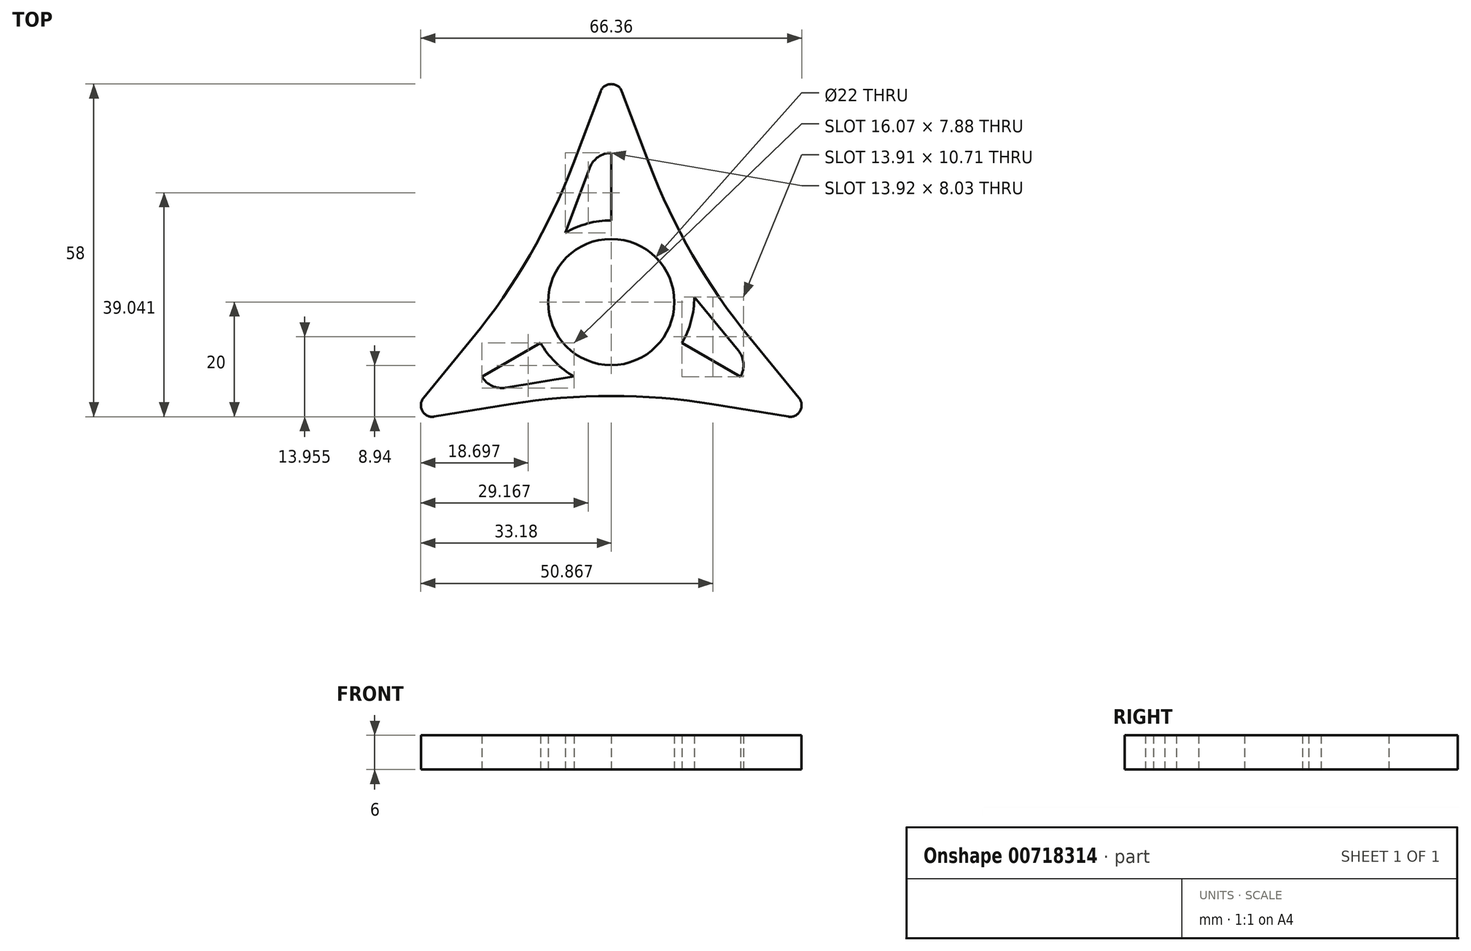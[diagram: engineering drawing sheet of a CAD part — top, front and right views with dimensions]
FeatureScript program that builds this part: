
annotation { "Feature Type Name" : "Feature", "Feature Type Description" : "" }
export const myFeature = defineFeature(function(context is Context, id is Id, definition is map)
    precondition{}
    {
        {
            var Q0;
            Q0=qCreatedBy(makeId("Top.planeOp"),FACE);
            var sketch = newSketch(context, id + "F0", { "sketchPlane" : qUnion([Q0])});
            skLineSegment(sketch, "E0", {"start": v(0, 36) * mm, "end": v(0, -37) * mm, "construction": true});
            skCircle(sketch, "E1", {"center": v(0, 0) * mm, "radius": 11 * mm});
            skCircle(sketch, "E2", {"center": v(0, 36) * mm, "radius": 2 * mm});
            skLineSegment(sketch, "E3", {"start": v(-1.87, 36.7) * mm, "end": v(-6.63, 24.1) * mm});
            skLineSegment(sketch, "E4.MirrorCS", {"start": v(1.87, 36.7) * mm, "end": v(6.63, 24.1) * mm});
            skLineSegment(sketch, "E5.1.0", {"start": v(-32.72, -16.73) * mm, "end": v(-24.2, -6.3) * mm});
            skLineSegment(sketch, "E5.1.1", {"start": v(-30.85, -19.97) * mm, "end": v(-17.56, -17.8) * mm});
            skCircle(sketch, "E5.1.2", {"center": v(-31.18, -18) * mm, "radius": 2 * mm});
            skLineSegment(sketch, "E5.2.0", {"start": v(30.85, -19.97) * mm, "end": v(17.56, -17.8) * mm});
            skLineSegment(sketch, "E5.2.1", {"start": v(32.72, -16.73) * mm, "end": v(24.2, -6.3) * mm});
            skCircle(sketch, "E5.2.2", {"center": v(31.18, -18) * mm, "radius": 2 * mm});
            skArc(sketch, "E6", {"start": v(-24.2, -6.3) * mm, "mid": v(-14.18, 8.19) * mm, "end": v(-6.63, 24.1) * mm});
            skArc(sketch, "E7.1.0", {"start": v(17.56, -17.8) * mm, "mid": v(0, -16.37) * mm, "end": v(-17.56, -17.8) * mm});
            skArc(sketch, "E7.2.0", {"start": v(6.63, 24.1) * mm, "mid": v(14.18, 8.19) * mm, "end": v(24.2, -6.3) * mm});
            skPoint(sketch, "E8.trimOffspring.end.orphan", {"position": v(-15.86, 3.15) * mm});
            skLineSegment(sketch, "E9.trimOffspring", {"start": v(-1.35, -14.7) * mm, "end": v(-3.63, -14.33) * mm});
            skLineSegment(sketch, "E10.trimOffspring", {"start": v(1.35, -14.7) * mm, "end": v(3.63, -14.33) * mm});
            skPoint(sketch, "E11.trimOffspring.end.orphan", {"position": v(15.86, 3.15) * mm});
            skArc(sketch, "E12", {"start": v(0, 26) * mm, "mid": v(-2.27, 25.3) * mm, "end": v(-3.74, 23.41) * mm});
            skLineSegment(sketch, "E13", {"start": v(-3.74, 23.41) * mm, "end": v(-8.03, 12.08) * mm});
            skPoint(sketch, "E14.MirrorCS.end.orphan", {"position": v(8.03, 12.08) * mm});
            skPoint(sketch, "E15.orphan", {"position": v(3.74, 23.41) * mm});
            skLineSegment(sketch, "E16", {"start": v(0, 26) * mm, "end": v(0, 14.24) * mm});
            skArc(sketch, "E17.trimOffspring", {"start": v(0, 14.24) * mm, "mid": v(-4.16, 13.7) * mm, "end": v(-8.03, 12.08) * mm});
            skArc(sketch, "E18.trimOffspring", {"start": v(-1.35, -14.7) * mm, "mid": v(0, -14.76) * mm, "end": v(1.35, -14.7) * mm});
            skArc(sketch, "E19.1.0", {"start": v(-22.52, -13) * mm, "mid": v(-20.77, -14.61) * mm, "end": v(-18.4, -14.95) * mm});
            skLineSegment(sketch, "E19.1.1", {"start": v(-18.4, -14.95) * mm, "end": v(-6.45, -13) * mm});
            skArc(sketch, "E19.1.2", {"start": v(-12.33, -7.12) * mm, "mid": v(-9.78, -10.44) * mm, "end": v(-6.45, -13) * mm});
            skArc(sketch, "E19.2.0", {"start": v(22.52, -13) * mm, "mid": v(23.04, -10.68) * mm, "end": v(22.15, -8.47) * mm});
            skLineSegment(sketch, "E19.2.1", {"start": v(22.15, -8.47) * mm, "end": v(14.48, 0.9) * mm});
            skArc(sketch, "E19.2.2", {"start": v(12.33, -7.12) * mm, "mid": v(13.93, -3.25) * mm, "end": v(14.48, 0.9) * mm});
            skLineSegment(sketch, "E20", {"start": v(12.33, -7.12) * mm, "end": v(22.52, -13) * mm});
            skLineSegment(sketch, "E21", {"start": v(-22.52, -13) * mm, "end": v(-12.33, -7.12) * mm});
            skSolve(sketch);
        }
        {
            var Q0;
            {var subQ18=sQuery(id+"F0.wireOp",EDGE,"E3");Q0=makeQuery(id+"F0.imprint","IMPRINT",FACE,{"disambiguationData":[TD([[makeQuery(id+"F0.imprint","IMPRINT",EDGE,{"derivedFrom":subQ18}),1.0]])]});}
            var Q1;
            {var subQ0=sQuery(id+"F0.wireOp",EDGE,"E2");var subQ1=makeQuery(id+"F0.imprint","INTERSECT",VERTEX,{"derivedFrom":[subQ0,sQuery(id+"F0.wireOp",EDGE,"E3")]});Q1=makeQuery(id+"F0.imprint","IMPRINT",FACE,{"disambiguationData":[TD([[makeQuery(id+"F0.imprint","IMPRINT",EDGE,{"disambiguationData":[TD([[subQ1,1.0]])],"derivedFrom":subQ0}),1.0]])]});}
            var Q2;
            {var subQ0=sQuery(id+"F0.wireOp",EDGE,"E5.2.2");var subQ1=makeQuery(id+"F0.imprint","INTERSECT",VERTEX,{"derivedFrom":[sQuery(id+"F0.wireOp",EDGE,"E5.2.0"),subQ0]});Q2=makeQuery(id+"F0.imprint","IMPRINT",FACE,{"disambiguationData":[TD([[makeQuery(id+"F0.imprint","IMPRINT",EDGE,{"disambiguationData":[TD([[subQ1,-1.0]])],"derivedFrom":subQ0}),1.0]])]});}
            var Q3;
            {var subQ0=sQuery(id+"F0.wireOp",EDGE,"E5.1.2");var subQ1=makeQuery(id+"F0.imprint","INTERSECT",VERTEX,{"derivedFrom":[sQuery(id+"F0.wireOp",EDGE,"E5.1.0"),subQ0]});Q3=makeQuery(id+"F0.imprint","IMPRINT",FACE,{"disambiguationData":[TD([[makeQuery(id+"F0.imprint","IMPRINT",EDGE,{"disambiguationData":[TD([[subQ1,-1.0]])],"derivedFrom":subQ0}),1.0]])]});}
            var Q4;
            {var subQ3=sQuery(id+"F0.wireOp",EDGE,"xdu3I85A-ipYB-XAy0-vIqM-tRquxRaiHgsL");var subQ5=makeQuery(id+"F0.imprint","IMPRINT",VERTEX,{"disambiguationData":[OD(0.0)],"derivedFrom":subQ3});Q4=makeQuery(id+"F0.imprint","IMPRINT",FACE,{"disambiguationData":[TD([[makeQuery(id+"F0.imprint","IMPRINT",EDGE,{"disambiguationData":[TD([[subQ5,-1.0]])],"derivedFrom":subQ3}),1.0]])]});}
            var Q5;
            Q5=makeQuery(id+"F0.imprint","IMPRINT",FACE,{"disambiguationData":[TD([[makeQuery(id+"F0.imprint","IMPRINT",EDGE,{"derivedFrom":sQuery(id+"F0.wireOp",EDGE,"E1")}),-1.0]])]});
            var Q6;
            {var subQ0=sQuery(id+"F0.wireOp",EDGE,"bd8721df-f465-4034-8980-84a94833bf2e.2.0");var subQ1=sQuery(id+"F0.wireOp",EDGE,"xdu3I85A-ipYB-XAy0-vIqM-tRquxRaiHgsL");var subQ3=makeQuery(id+"F0.imprint","INTERSECT",VERTEX,{"derivedFrom":[subQ1,subQ0]});Q6=makeQuery(id+"F0.imprint","IMPRINT",FACE,{"disambiguationData":[TD([[makeQuery(id+"F0.imprint","IMPRINT",EDGE,{"disambiguationData":[TD([[subQ3,-1.0]])],"derivedFrom":subQ1}),1.0]])]});}
            var Q7;
            {var subQ0=sQuery(id+"F0.wireOp",EDGE,"E14.MirrorCS");var subQ1=sQuery(id+"F0.wireOp",EDGE,"xdu3I85A-ipYB-XAy0-vIqM-tRquxRaiHgsL");var subQ3=makeQuery(id+"F0.imprint","INTERSECT",VERTEX,{"derivedFrom":[subQ1,subQ0]});Q7=makeQuery(id+"F0.imprint","IMPRINT",FACE,{"disambiguationData":[TD([[makeQuery(id+"F0.imprint","IMPRINT",EDGE,{"disambiguationData":[TD([[subQ3,1.0]])],"derivedFrom":subQ1}),1.0]])]});}
            var Q8;
            {var subQ0=sQuery(id+"F0.wireOp",EDGE,"bd8721df-f465-4034-8980-84a94833bf2e.1.2");var subQ1=sQuery(id+"F0.wireOp",EDGE,"xdu3I85A-ipYB-XAy0-vIqM-tRquxRaiHgsL");var subQ3=makeQuery(id+"F0.imprint","INTERSECT",VERTEX,{"derivedFrom":[subQ1,subQ0]});Q8=makeQuery(id+"F0.imprint","IMPRINT",FACE,{"disambiguationData":[TD([[makeQuery(id+"F0.imprint","IMPRINT",EDGE,{"disambiguationData":[TD([[subQ3,1.0]])],"derivedFrom":subQ1}),1.0]])]});}
            var Q9;
            {var subQ0=sQuery(id+"F0.wireOp",EDGE,"E13");var subQ1=sQuery(id+"F0.wireOp",EDGE,"xdu3I85A-ipYB-XAy0-vIqM-tRquxRaiHgsL");var subQ3=makeQuery(id+"F0.imprint","INTERSECT",VERTEX,{"derivedFrom":[subQ1,subQ0]});Q9=makeQuery(id+"F0.imprint","IMPRINT",FACE,{"disambiguationData":[TD([[makeQuery(id+"F0.imprint","IMPRINT",EDGE,{"disambiguationData":[TD([[subQ3,-1.0]])],"derivedFrom":subQ1}),1.0]])]});}
            extrude(context, id + "F1", {"entities" : qUnion([Q0, Q1, Q2, Q3, Q4, Q5, Q6, Q7, Q8, Q9]), "depth" : 6 * mm, "offsetDistance" : 25 * mm});
        }
    });
